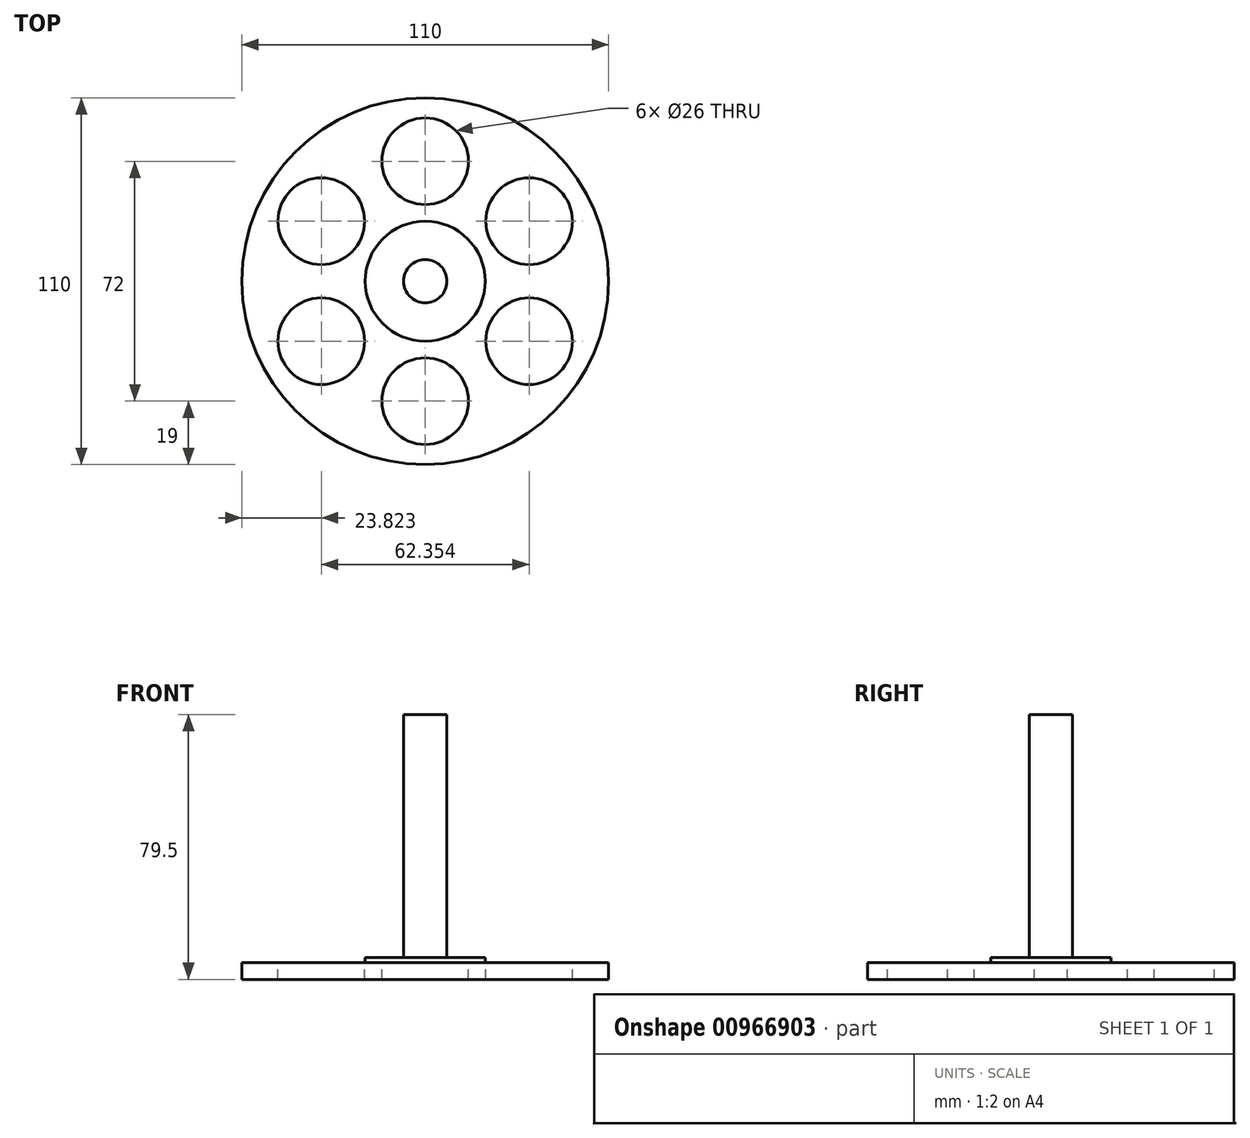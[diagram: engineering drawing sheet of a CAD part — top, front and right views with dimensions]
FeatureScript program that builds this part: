
annotation { "Feature Type Name" : "Feature", "Feature Type Description" : "" }
export const myFeature = defineFeature(function(context is Context, id is Id, definition is map)
    precondition{}
    {
        {
            var Q0;
            Q0=qCreatedBy(makeId("Top.planeOp"),FACE);
            var sketch = newSketch(context, id + "F0", { "sketchPlane" : qUnion([Q0])});
            skCircle(sketch, "E0", {"center": v(0, 0) * mm, "radius": 55 * mm});
            skSolve(sketch);
        }
        {
            var Q0;
            Q0 = qSketchRegion(id + "F0", true);
            extrude(context, id + "F1", {"entities" : qUnion([Q0]), "depth" : 5 * mm, "offsetDistance" : 25 * mm});
        }
        {
            var Q0;
            Q0=makeQuery(id+"F1.opExtrude","CAP_FACE",FACE,{"disambiguationData":[OSD([sQuery(id+"F0.wireOp",EDGE,"E0")])],"isStart":false});
            var sketch = newSketch(context, id + "F2", { "sketchPlane" : qUnion([Q0])});
            skCircle(sketch, "E1", {"center": v(0, 0) * mm, "radius": 18 * mm});
            skSolve(sketch);
        }
        {
            var Q0;
            Q0 = qSketchRegion(id + "F2", true);
            extrude(context, id + "F3", {"entities" : qUnion([Q0]), "operationType" : NewBodyOperationType.ADD, "depth" : 1.5 * mm, "offsetDistance" : 25 * mm});
        }
        {
            var Q0;
            Q0=makeQuery(id+"F3.opExtrude","CAP_FACE",FACE,{"disambiguationData":[OSD([sQuery(id+"F2.wireOp",EDGE,"E1")])],"isStart":false});
            var sketch = newSketch(context, id + "F4", { "sketchPlane" : qUnion([Q0])});
            skCircle(sketch, "E2", {"center": v(0, 0) * mm, "radius": 6.5 * mm});
            skSolve(sketch);
        }
        {
            var Q0;
            Q0 = qSketchRegion(id + "F4", true);
            extrude(context, id + "F5", {"entities" : qUnion([Q0]), "operationType" : NewBodyOperationType.ADD, "depth" : 73 * mm, "offsetDistance" : 25 * mm});
        }
        {
            var Q0;
            Q0=makeQuery(id+"F1.opExtrude","CAP_FACE",FACE,{"disambiguationData":[OSD([sQuery(id+"F0.wireOp",EDGE,"E0")])],"isStart":false});
            var sketch = newSketch(context, id + "F6", { "sketchPlane" : qUnion([Q0])});
            skCircle(sketch, "E3", {"center": v(0, 36) * mm, "radius": 13 * mm});
            skCircle(sketch, "E4.1.0", {"center": v(-31.18, 18) * mm, "radius": 13 * mm});
            skCircle(sketch, "E4.2.0", {"center": v(-31.18, -18) * mm, "radius": 13 * mm});
            skCircle(sketch, "E4.3.0", {"center": v(0, -36) * mm, "radius": 13 * mm});
            skCircle(sketch, "E4.4.0", {"center": v(31.18, -18) * mm, "radius": 13 * mm});
            skCircle(sketch, "E4.5.0", {"center": v(31.18, 18) * mm, "radius": 13 * mm});
            skPoint(sketch, "E4.center", {"position": v(0, 0) * mm});
            skSolve(sketch);
        }
        {
            var Q0;
            Q0 = qSketchRegion(id + "F6", true);
            extrude(context, id + "F7", {"entities" : qUnion([Q0]), "operationType" : NewBodyOperationType.REMOVE, "endBound" : BoundingType.THROUGH_ALL, "oppositeDirection" : true, "depth" : 25 * mm, "offsetDistance" : 25 * mm});
        }
    });
